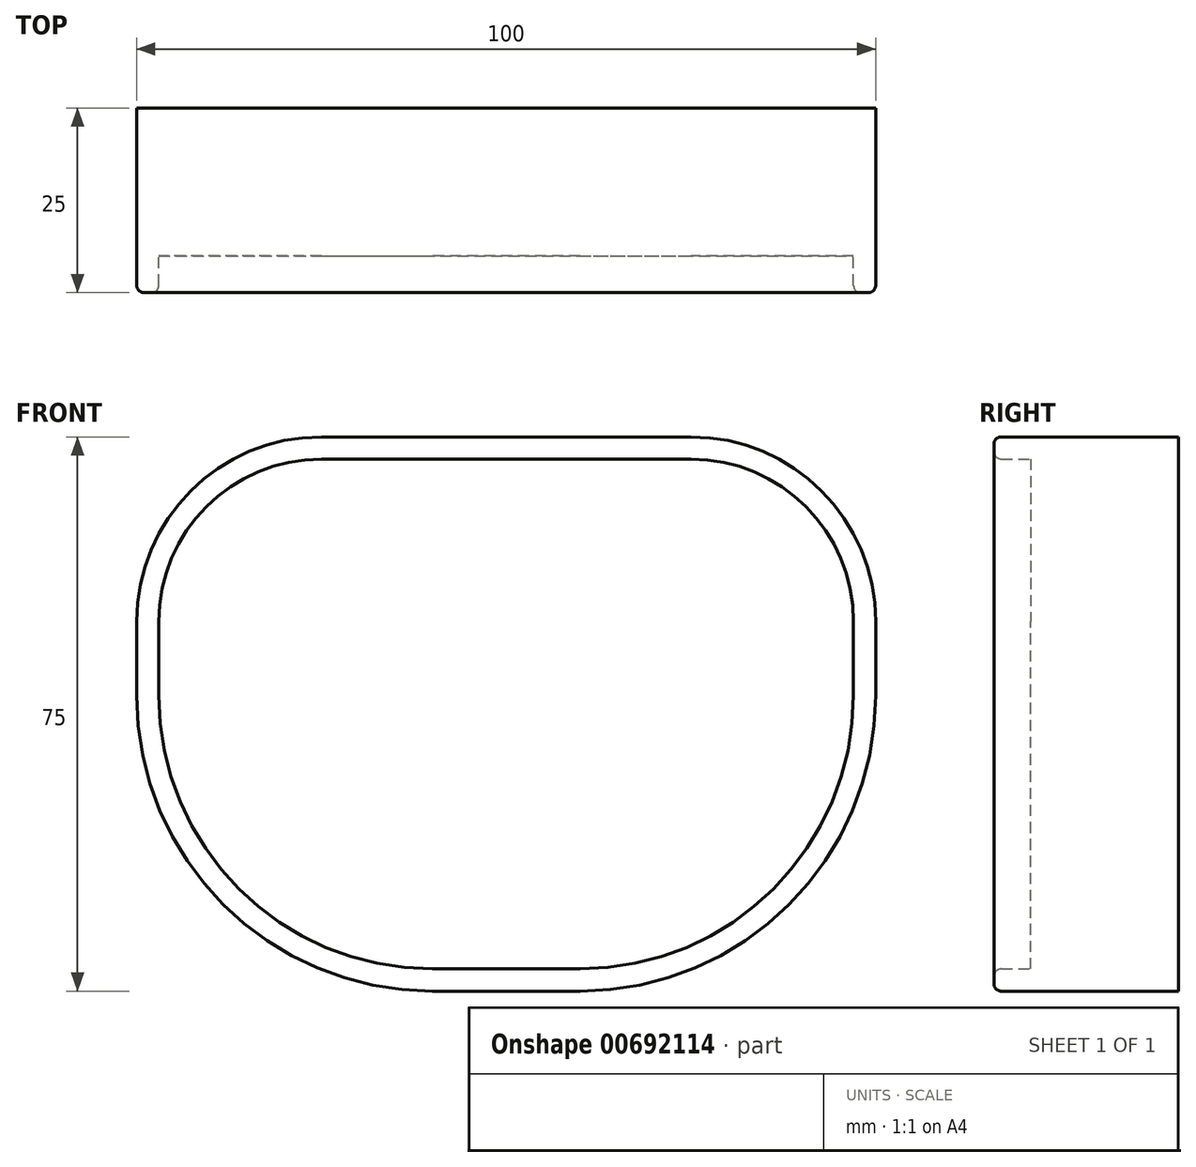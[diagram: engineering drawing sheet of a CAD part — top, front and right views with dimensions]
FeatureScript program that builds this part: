
annotation { "Feature Type Name" : "Feature", "Feature Type Description" : "" }
export const myFeature = defineFeature(function(context is Context, id is Id, definition is map)
    precondition{}
    {
        {
            var Q0;
            Q0=qCreatedBy(makeId("Front.planeOp"),FACE);
            var sketch = newSketch(context, id + "F0", { "sketchPlane" : qUnion([Q0])});
            skLineSegment(sketch, "E0.right", {"start": v(-54.81, 5) * mm, "end": v(-54.81, 5) * mm});
            skPoint(sketch, "E1.visualSharp", {"position": v(-54.81, 30) * mm});
            skPoint(sketch, "E2.visualSharp", {"position": v(45.19, -30) * mm});
            skPoint(sketch, "E3.visualSharp", {"position": v(-54.81, -30) * mm});
            skLineSegment(sketch, "E4.left", {"start": v(50, -5) * mm, "end": v(50, 5) * mm});
            skLineSegment(sketch, "E4.right", {"start": v(-50, -5) * mm, "end": v(-50, 5) * mm});
            skLineSegment(sketch, "E5", {"start": v(-25, 30) * mm, "end": v(25, 30) * mm});
            skLineSegment(sketch, "E6", {"start": v(10, -45) * mm, "end": v(-10, -45) * mm});
            skPoint(sketch, "E7.visualSharp", {"position": v(-50, 30) * mm});
            skArc(sketch, "E7.filletArc", {"start": v(-25, 30) * mm, "mid": v(-42.68, 22.68) * mm, "end": v(-50, 5) * mm});
            skPoint(sketch, "E8.visualSharp", {"position": v(50, 30) * mm});
            skArc(sketch, "E8.filletArc", {"start": v(50, 5) * mm, "mid": v(42.68, 22.68) * mm, "end": v(25, 30) * mm});
            skPoint(sketch, "E9.visualSharp", {"position": v(-50, -45) * mm});
            skArc(sketch, "E9.filletArc", {"start": v(-50, -5) * mm, "mid": v(-38.28, -33.28) * mm, "end": v(-10, -45) * mm});
            skPoint(sketch, "E10.visualSharp", {"position": v(50, -45) * mm});
            skArc(sketch, "E10.filletArc", {"start": v(10, -45) * mm, "mid": v(38.28, -33.28) * mm, "end": v(50, -5) * mm});
            skLineSegment(sketch, "E11.0", {"start": v(-25, 27) * mm, "end": v(25, 27) * mm});
            skArc(sketch, "E12.0", {"start": v(47, 5) * mm, "mid": v(40.56, 20.56) * mm, "end": v(25, 27) * mm});
            skLineSegment(sketch, "E13.0", {"start": v(47, -5) * mm, "end": v(47, 5) * mm});
            skLineSegment(sketch, "E14.0", {"start": v(-47, -5) * mm, "end": v(-47, 5) * mm});
            skArc(sketch, "E15.0", {"start": v(-25, 27) * mm, "mid": v(-40.56, 20.56) * mm, "end": v(-47, 5) * mm});
            skArc(sketch, "E16.0", {"start": v(-47, -5) * mm, "mid": v(-36.16, -31.16) * mm, "end": v(-10, -42) * mm});
            skLineSegment(sketch, "E17.0", {"start": v(10, -42) * mm, "end": v(-10, -42) * mm});
            skArc(sketch, "E18.0", {"start": v(10, -42) * mm, "mid": v(36.16, -31.16) * mm, "end": v(47, -5) * mm});
            skSolve(sketch);
        }
        {
            var Q0;
            Q0=makeQuery(id+"F0.imprint","IMPRINT",FACE,{"disambiguationData":[TD([[makeQuery(id+"F0.imprint","IMPRINT",EDGE,{"derivedFrom":sQuery(id+"F0.wireOp",EDGE,"E11.0")}),-1.0]])]});
            extrude(context, id + "F1", {"entities" : qUnion([Q0]), "depth" : 20 * mm, "offsetDistance" : 25 * mm});
        }
        {
            var Q0;
            Q0 = qSketchRegion(id + "F0", true);
            extrude(context, id + "F2", {"entities" : qUnion([Q0]), "operationType" : NewBodyOperationType.ADD, "depth" : 25 * mm, "offsetDistance" : 25 * mm});
        }
        {
            var Q0;
            Q0=makeQuery(id+"F2.opExtrude","CAP_EDGE",EDGE,{"disambiguationData":[OSD([sQuery(id+"F0.wireOp",EDGE,"E11.0")])],"isStart":false});
            var Q1;
            Q1=makeQuery(id+"F2.opExtrude","CAP_EDGE",EDGE,{"disambiguationData":[OSD([sQuery(id+"F0.wireOp",EDGE,"E10.filletArc")])],"isStart":false});
            fillet(context, id + "F3", {"entities" : qUnion([Q0, Q1]), "radius" : 1 * mm, "tangentPropagation" : true, "allowEdgeOverflow" : false});
        }
    });
